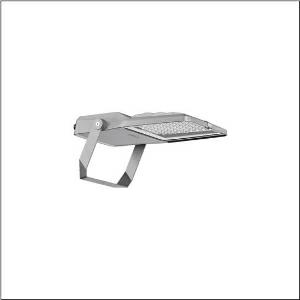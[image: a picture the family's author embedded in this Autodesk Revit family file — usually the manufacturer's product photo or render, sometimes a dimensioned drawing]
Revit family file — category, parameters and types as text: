
# Revit family: floodlight_fl_21_mini___pl52_5xa7776d4d1a_fa17
name_source: partatom
category: Lighting Fixtures
units: mm (PartAtom-declared; Revit-internal decimal feet)

## family parameters
Cut with Voids When Loaded = No
Host = Face
Light Source = No
Part Type = Normal
Room Calculation Point = No
Round Connector Dimension = Use Diameter
Shared = No

## types (1)
- --- (1 x LED, 18600 lm, 142.9 W, 4000K)
    Apparent Load = 143 VA
    CIE Flux Codes = 26 60 98 100 100
    Color Rendering = 70
    Color Temperature = 4000K
    Default Elevation = 1800 mm
    Description = Floodlight FL 21 mini, floodlight, primary light control with lens, of PMMA, primary optical cover: protective disc, of toughened safety glass, transparent, light distribution: PL52, light emission: direct distribution, installation type: surface-mounted, LED, High Power LED, rated luminous flux: 18.600lm, luminous efficacy: 130lm/W, light colour: 740, colour temperature: 4000K, control gear: D4iSmart Interface (Zhaga), control: overheat protection, constant luminous flux control, time-dependent luminous flux control, flexible luminous flux parameterisation, pre-setting: logarithmic dimming characteristic, with terminal, 6-pole, mains connection: 220..240V, AC, 50/60Hz, start of lifetime: 143W, end of service life: 151W, reduction: 63W, mounting bracket, of diecast aluminium, powder-coated, Siteco® metallic grey (DB 702S), corrosivity category C5 mid according to DIN EN ISO 12944, suitable for swimming pools, chlorine-resistant, sealing non-destructively replaceable, mounting bracket, of steel, galvanised, powder-coated, Siteco® metallic grey (DB 702S), Smart Interface below and above, protection rating (complete): IP66, insulation class (complete): insulation class II (safety insulation), certification: CE, ENEC, VDE, protection symbol: D, impact resistance: IK08, permissible operating ambient temperature: -40..+40°C, permissible operating ambient temperature for outdoor applications: -40..+50°C, standard: DIN EN 12944, LABS conformity tested according to VDMA 24364:2018-05, packaging unit: 1 piece

Light Distribution: PL52
    Height = 70 mm
    Lamp = 1 x LED
    Lamp Light Flux = 18600 lm
    Lamp Power = 142.9 W
    Lamp count = 1
    Length = 485 mm
    Luminous efficacy = 130 lm/W
    Manufacturer = Siteco
    ModVariant = No
    Model = 5XA7776D4D1A
    Number of Poles = 1
    OnlyDefault = Yes
    Power Factor = 1
    Product Name = Floodlight FL 21 mini | PL52
    Product group = floodlight | pylon annexe
    ProductGroupID = 6200
    Protection Class = Protection class II
    Protection Degree = IP 66
    RLX_Detail_Level = 1
    RLX_Emergency_Light_Flux = 0 lm
    RLX_Emergency_Type = 0
    RLX_Emergency_Type_DB = No
    RlxData = <blob elided: 96425 chars, md5=d00037c4>
    Socket = socket
    Standby Power = 0 W
    System Light Flux = 18600 lm
    System Power = 143 W
    Type Comments = factory setting: luminous flux: 100 % | dim-lin: 254 | 730 mA
    Type Image = l_1006845.jpg
    URL = http://relux.com
    VarID = @adj_095372
    Voltage = 0 V
    Weight = 0.00 kg
    Width = 337 mm

## geometry (parser evidence)
native form markers: Blend x4, Sweep x12
no freeform markers — native parametric forms only
